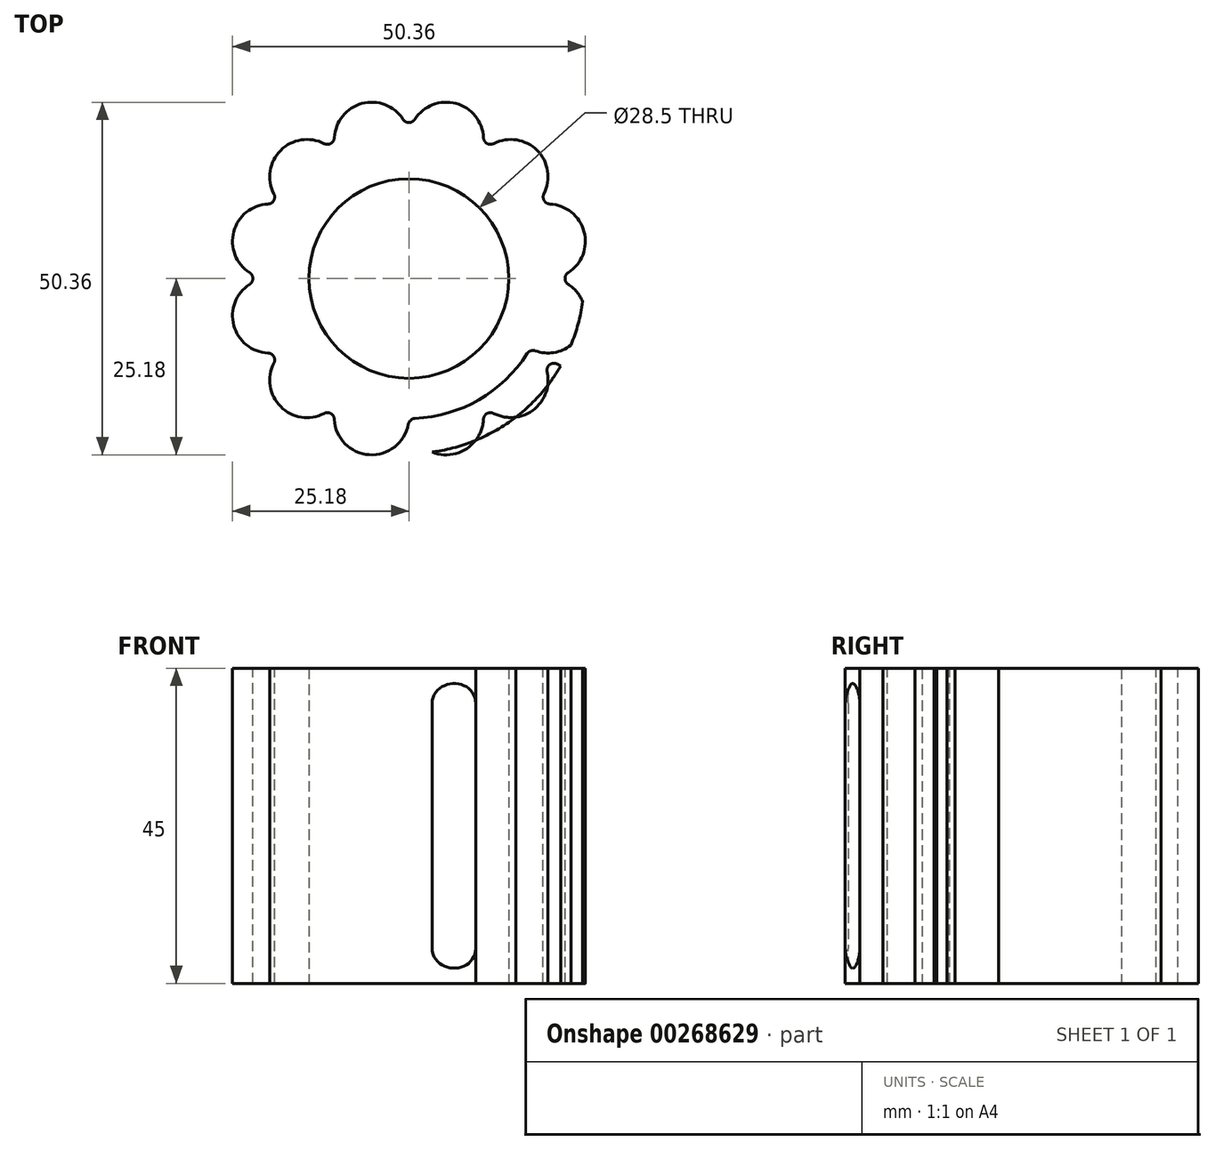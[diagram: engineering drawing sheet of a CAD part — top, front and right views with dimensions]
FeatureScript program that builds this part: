
annotation { "Feature Type Name" : "Feature", "Feature Type Description" : "" }
export const myFeature = defineFeature(function(context is Context, id is Id, definition is map)
    precondition{}
    {
        {
            var Q0;
            Q0=qCreatedBy(makeId("Top.planeOp"),FACE);
            var sketch = newSketch(context, id + "F0", { "sketchPlane" : qUnion([Q0])});
            skCircle(sketch, "E0", {"center": v(0, 0) * mm, "radius": 22.5 * mm});
            skCircle(sketch, "E1", {"center": v(0, 0) * mm, "radius": 14.25 * mm});
            skCircle(sketch, "E2.cCircle", {"center": v(0, 0) * mm, "radius": 22.5 * mm, "construction": true});
            skCircle(sketch, "E3", {"center": v(0, 0) * mm, "radius": 20 * mm});
            skCircle(sketch, "E4.cCircle", {"center": v(0, 0) * mm, "radius": 20 * mm, "construction": true});
            skCircle(sketch, "E5", {"center": v(0, 0) * mm, "radius": 25 * mm});
            skPoint(sketch, "E6.0.midPoint", {"position": v(22.5, 0) * mm});
            skLineSegment(sketch, "E7", {"start": v(-22.5, 12.99) * mm, "end": v(22.5, -12.99) * mm});
            skPoint(sketch, "E8.0.midPoint", {"position": v(11.25, 19.49) * mm});
            skCircle(sketch, "E9.cCircle", {"center": v(0, 0) * mm, "radius": 25 * mm, "construction": true});
            skPoint(sketch, "E9.0.midPoint", {"position": v(0, 25) * mm});
            skArc(sketch, "E10", {"start": v(10, 17.32) * mm, "mid": v(6.7, 25) * mm, "end": v(0, 20) * mm});
            skArc(sketch, "E11", {"start": v(17.32, 10) * mm, "mid": v(18.3, 18.3) * mm, "end": v(10, 17.32) * mm});
            skArc(sketch, "E12", {"start": v(20, 0) * mm, "mid": v(25, 6.7) * mm, "end": v(17.32, 10) * mm});
            skArc(sketch, "E13", {"start": v(17.32, -10) * mm, "mid": v(25, -6.7) * mm, "end": v(20, 0) * mm});
            skArc(sketch, "E14", {"start": v(10, -17.32) * mm, "mid": v(18.3, -18.3) * mm, "end": v(17.32, -10) * mm});
            skArc(sketch, "E15", {"start": v(0, -20) * mm, "mid": v(6.7, -25) * mm, "end": v(10, -17.32) * mm});
            skArc(sketch, "E16", {"start": v(-10, -17.32) * mm, "mid": v(-6.7, -25) * mm, "end": v(0, -20) * mm});
            skArc(sketch, "E17", {"start": v(-17.32, -10) * mm, "mid": v(-18.3, -18.3) * mm, "end": v(-10, -17.32) * mm});
            skArc(sketch, "E18", {"start": v(-20, 0) * mm, "mid": v(-25, -6.7) * mm, "end": v(-17.32, -10) * mm});
            skArc(sketch, "E19", {"start": v(-17.32, 10) * mm, "mid": v(-25, 6.7) * mm, "end": v(-20, 0) * mm});
            skArc(sketch, "E20", {"start": v(-10, 17.32) * mm, "mid": v(-18.3, 18.3) * mm, "end": v(-17.32, 10) * mm});
            skArc(sketch, "E21", {"start": v(0, 20) * mm, "mid": v(-6.7, 25) * mm, "end": v(-10, 17.32) * mm});
            skSolve(sketch);
        }
        {
            var Q0;
            {var subQ0=sQuery(id+"F0.wireOp",EDGE,"E20");var subQ1=sQuery(id+"F0.wireOp",EDGE,"E5");var subQ2=makeQuery(id+"F0.imprint","INTERSECT",VERTEX,{"disambiguationData":[OD(0.0)],"derivedFrom":[subQ1,subQ0]});Q0=makeQuery(id+"F0.imprint","IMPRINT",FACE,{"disambiguationData":[TD([[makeQuery(id+"F0.imprint","IMPRINT",EDGE,{"disambiguationData":[TD([[subQ2,-1.0]])],"derivedFrom":subQ1}),-1.0]])]});}
            var Q1;
            {var subQ0=sQuery(id+"F0.wireOp",EDGE,"E20");var subQ1=sQuery(id+"F0.wireOp",EDGE,"E0");var subQ2=makeQuery(id+"F0.imprint","INTERSECT",VERTEX,{"disambiguationData":[OD(0.0)],"derivedFrom":[subQ1,subQ0]});Q1=makeQuery(id+"F0.imprint","IMPRINT",FACE,{"disambiguationData":[TD([[makeQuery(id+"F0.imprint","IMPRINT",EDGE,{"disambiguationData":[TD([[subQ2,-1.0]])],"derivedFrom":subQ1}),-1.0]])]});}
            var Q2;
            {var subQ0=sQuery(id+"F0.wireOp",EDGE,"E20");var subQ1=sQuery(id+"F0.wireOp",EDGE,"E0");var subQ2=makeQuery(id+"F0.imprint","INTERSECT",VERTEX,{"disambiguationData":[OD(0.0)],"derivedFrom":[subQ1,subQ0]});Q2=makeQuery(id+"F0.imprint","IMPRINT",FACE,{"disambiguationData":[TD([[makeQuery(id+"F0.imprint","IMPRINT",EDGE,{"disambiguationData":[TD([[subQ2,-1.0]])],"derivedFrom":subQ1}),1.0]])]});}
            var Q3;
            {var subQ10=sQuery(id+"F0.wireOp",EDGE,"E7");var subQ12=sQuery(id+"F0.wireOp",EDGE,"E1");var subQ13=makeQuery(id+"F0.imprint","INTERSECT",VERTEX,{"disambiguationData":[OD(0.0)],"derivedFrom":[subQ12,subQ10]});Q3=makeQuery(id+"F0.imprint","IMPRINT",FACE,{"disambiguationData":[TD([[makeQuery(id+"F0.imprint","IMPRINT",EDGE,{"disambiguationData":[TD([[subQ13,1.0]])],"derivedFrom":subQ12}),-1.0]])]});}
            var Q4;
            {var subQ0=sQuery(id+"F0.wireOp",EDGE,"E19");var subQ1=sQuery(id+"F0.wireOp",EDGE,"E5");var subQ2=makeQuery(id+"F0.imprint","INTERSECT",VERTEX,{"disambiguationData":[OD(0.0)],"derivedFrom":[subQ1,subQ0]});Q4=makeQuery(id+"F0.imprint","IMPRINT",FACE,{"disambiguationData":[TD([[makeQuery(id+"F0.imprint","IMPRINT",EDGE,{"disambiguationData":[TD([[subQ2,-1.0]])],"derivedFrom":subQ1}),-1.0]])]});}
            var Q5;
            {var subQ0=sQuery(id+"F0.wireOp",EDGE,"E19");var subQ1=sQuery(id+"F0.wireOp",EDGE,"E0");var subQ2=makeQuery(id+"F0.imprint","INTERSECT",VERTEX,{"disambiguationData":[OD(0.0)],"derivedFrom":[subQ1,subQ0]});Q5=makeQuery(id+"F0.imprint","IMPRINT",FACE,{"disambiguationData":[TD([[makeQuery(id+"F0.imprint","IMPRINT",EDGE,{"disambiguationData":[TD([[subQ2,-1.0]])],"derivedFrom":subQ1}),-1.0]])]});}
            var Q6;
            {var subQ0=sQuery(id+"F0.wireOp",EDGE,"E19");var subQ1=sQuery(id+"F0.wireOp",EDGE,"E0");var subQ2=makeQuery(id+"F0.imprint","INTERSECT",VERTEX,{"disambiguationData":[OD(0.0)],"derivedFrom":[subQ1,subQ0]});Q6=makeQuery(id+"F0.imprint","IMPRINT",FACE,{"disambiguationData":[TD([[makeQuery(id+"F0.imprint","IMPRINT",EDGE,{"disambiguationData":[TD([[subQ2,-1.0]])],"derivedFrom":subQ1}),1.0]])]});}
            var Q7;
            {var subQ0=sQuery(id+"F0.wireOp",EDGE,"E18");var subQ1=sQuery(id+"F0.wireOp",EDGE,"E5");var subQ2=makeQuery(id+"F0.imprint","INTERSECT",VERTEX,{"disambiguationData":[OD(0.0)],"derivedFrom":[subQ1,subQ0]});Q7=makeQuery(id+"F0.imprint","IMPRINT",FACE,{"disambiguationData":[TD([[makeQuery(id+"F0.imprint","IMPRINT",EDGE,{"disambiguationData":[TD([[subQ2,-1.0]])],"derivedFrom":subQ1}),-1.0]])]});}
            var Q8;
            {var subQ0=sQuery(id+"F0.wireOp",EDGE,"E18");var subQ1=sQuery(id+"F0.wireOp",EDGE,"E0");var subQ2=makeQuery(id+"F0.imprint","INTERSECT",VERTEX,{"disambiguationData":[OD(0.0)],"derivedFrom":[subQ1,subQ0]});Q8=makeQuery(id+"F0.imprint","IMPRINT",FACE,{"disambiguationData":[TD([[makeQuery(id+"F0.imprint","IMPRINT",EDGE,{"disambiguationData":[TD([[subQ2,-1.0]])],"derivedFrom":subQ1}),-1.0]])]});}
            var Q9;
            {var subQ0=sQuery(id+"F0.wireOp",EDGE,"E18");var subQ1=sQuery(id+"F0.wireOp",EDGE,"E0");var subQ2=makeQuery(id+"F0.imprint","INTERSECT",VERTEX,{"disambiguationData":[OD(0.0)],"derivedFrom":[subQ1,subQ0]});Q9=makeQuery(id+"F0.imprint","IMPRINT",FACE,{"disambiguationData":[TD([[makeQuery(id+"F0.imprint","IMPRINT",EDGE,{"disambiguationData":[TD([[subQ2,-1.0]])],"derivedFrom":subQ1}),1.0]])]});}
            var Q10;
            {var subQ0=sQuery(id+"F0.wireOp",EDGE,"E17");var subQ1=sQuery(id+"F0.wireOp",EDGE,"E5");var subQ2=makeQuery(id+"F0.imprint","INTERSECT",VERTEX,{"disambiguationData":[OD(0.0)],"derivedFrom":[subQ1,subQ0]});Q10=makeQuery(id+"F0.imprint","IMPRINT",FACE,{"disambiguationData":[TD([[makeQuery(id+"F0.imprint","IMPRINT",EDGE,{"disambiguationData":[TD([[subQ2,-1.0]])],"derivedFrom":subQ1}),-1.0]])]});}
            var Q11;
            {var subQ0=sQuery(id+"F0.wireOp",EDGE,"E17");var subQ1=sQuery(id+"F0.wireOp",EDGE,"E0");var subQ2=makeQuery(id+"F0.imprint","INTERSECT",VERTEX,{"disambiguationData":[OD(0.0)],"derivedFrom":[subQ1,subQ0]});Q11=makeQuery(id+"F0.imprint","IMPRINT",FACE,{"disambiguationData":[TD([[makeQuery(id+"F0.imprint","IMPRINT",EDGE,{"disambiguationData":[TD([[subQ2,-1.0]])],"derivedFrom":subQ1}),-1.0]])]});}
            var Q12;
            {var subQ0=sQuery(id+"F0.wireOp",EDGE,"E17");var subQ1=sQuery(id+"F0.wireOp",EDGE,"E0");var subQ2=makeQuery(id+"F0.imprint","INTERSECT",VERTEX,{"disambiguationData":[OD(0.0)],"derivedFrom":[subQ1,subQ0]});Q12=makeQuery(id+"F0.imprint","IMPRINT",FACE,{"disambiguationData":[TD([[makeQuery(id+"F0.imprint","IMPRINT",EDGE,{"disambiguationData":[TD([[subQ2,-1.0]])],"derivedFrom":subQ1}),1.0]])]});}
            var Q13;
            {var subQ0=sQuery(id+"F0.wireOp",EDGE,"E21");var subQ1=sQuery(id+"F0.wireOp",EDGE,"E5");var subQ2=makeQuery(id+"F0.imprint","INTERSECT",VERTEX,{"disambiguationData":[OD(0.0)],"derivedFrom":[subQ1,subQ0]});Q13=makeQuery(id+"F0.imprint","IMPRINT",FACE,{"disambiguationData":[TD([[makeQuery(id+"F0.imprint","IMPRINT",EDGE,{"disambiguationData":[TD([[subQ2,-1.0]])],"derivedFrom":subQ1}),-1.0]])]});}
            var Q14;
            {var subQ0=sQuery(id+"F0.wireOp",EDGE,"E21");var subQ1=sQuery(id+"F0.wireOp",EDGE,"E0");var subQ2=makeQuery(id+"F0.imprint","INTERSECT",VERTEX,{"disambiguationData":[OD(0.0)],"derivedFrom":[subQ1,subQ0]});Q14=makeQuery(id+"F0.imprint","IMPRINT",FACE,{"disambiguationData":[TD([[makeQuery(id+"F0.imprint","IMPRINT",EDGE,{"disambiguationData":[TD([[subQ2,-1.0]])],"derivedFrom":subQ1}),-1.0]])]});}
            var Q15;
            {var subQ0=sQuery(id+"F0.wireOp",EDGE,"E21");var subQ1=sQuery(id+"F0.wireOp",EDGE,"E0");var subQ2=makeQuery(id+"F0.imprint","INTERSECT",VERTEX,{"disambiguationData":[OD(0.0)],"derivedFrom":[subQ1,subQ0]});Q15=makeQuery(id+"F0.imprint","IMPRINT",FACE,{"disambiguationData":[TD([[makeQuery(id+"F0.imprint","IMPRINT",EDGE,{"disambiguationData":[TD([[subQ2,-1.0]])],"derivedFrom":subQ1}),1.0]])]});}
            var Q16;
            {var subQ0=sQuery(id+"F0.wireOp",EDGE,"E10");var subQ1=sQuery(id+"F0.wireOp",EDGE,"E0");var subQ2=makeQuery(id+"F0.imprint","INTERSECT",VERTEX,{"disambiguationData":[OD(0.0)],"derivedFrom":[subQ1,subQ0]});Q16=makeQuery(id+"F0.imprint","IMPRINT",FACE,{"disambiguationData":[TD([[makeQuery(id+"F0.imprint","IMPRINT",EDGE,{"disambiguationData":[TD([[subQ2,-1.0]])],"derivedFrom":subQ1}),1.0]])]});}
            var Q17;
            {var subQ0=sQuery(id+"F0.wireOp",EDGE,"E10");var subQ1=sQuery(id+"F0.wireOp",EDGE,"E0");var subQ2=makeQuery(id+"F0.imprint","INTERSECT",VERTEX,{"disambiguationData":[OD(0.0)],"derivedFrom":[subQ1,subQ0]});Q17=makeQuery(id+"F0.imprint","IMPRINT",FACE,{"disambiguationData":[TD([[makeQuery(id+"F0.imprint","IMPRINT",EDGE,{"disambiguationData":[TD([[subQ2,-1.0]])],"derivedFrom":subQ1}),-1.0]])]});}
            var Q18;
            {var subQ0=sQuery(id+"F0.wireOp",EDGE,"E10");var subQ1=sQuery(id+"F0.wireOp",EDGE,"E5");var subQ2=makeQuery(id+"F0.imprint","INTERSECT",VERTEX,{"disambiguationData":[OD(0.0)],"derivedFrom":[subQ1,subQ0]});Q18=makeQuery(id+"F0.imprint","IMPRINT",FACE,{"disambiguationData":[TD([[makeQuery(id+"F0.imprint","IMPRINT",EDGE,{"disambiguationData":[TD([[subQ2,-1.0]])],"derivedFrom":subQ1}),-1.0]])]});}
            var Q19;
            {var subQ0=sQuery(id+"F0.wireOp",EDGE,"E11");var subQ1=sQuery(id+"F0.wireOp",EDGE,"E0");var subQ2=makeQuery(id+"F0.imprint","INTERSECT",VERTEX,{"disambiguationData":[OD(0.0)],"derivedFrom":[subQ1,subQ0]});Q19=makeQuery(id+"F0.imprint","IMPRINT",FACE,{"disambiguationData":[TD([[makeQuery(id+"F0.imprint","IMPRINT",EDGE,{"disambiguationData":[TD([[subQ2,-1.0]])],"derivedFrom":subQ1}),1.0]])]});}
            var Q20;
            {var subQ0=sQuery(id+"F0.wireOp",EDGE,"E11");var subQ1=sQuery(id+"F0.wireOp",EDGE,"E0");var subQ2=makeQuery(id+"F0.imprint","INTERSECT",VERTEX,{"disambiguationData":[OD(0.0)],"derivedFrom":[subQ1,subQ0]});Q20=makeQuery(id+"F0.imprint","IMPRINT",FACE,{"disambiguationData":[TD([[makeQuery(id+"F0.imprint","IMPRINT",EDGE,{"disambiguationData":[TD([[subQ2,-1.0]])],"derivedFrom":subQ1}),-1.0]])]});}
            var Q21;
            {var subQ0=sQuery(id+"F0.wireOp",EDGE,"E11");var subQ1=sQuery(id+"F0.wireOp",EDGE,"E5");var subQ2=makeQuery(id+"F0.imprint","INTERSECT",VERTEX,{"disambiguationData":[OD(0.0)],"derivedFrom":[subQ1,subQ0]});Q21=makeQuery(id+"F0.imprint","IMPRINT",FACE,{"disambiguationData":[TD([[makeQuery(id+"F0.imprint","IMPRINT",EDGE,{"disambiguationData":[TD([[subQ2,-1.0]])],"derivedFrom":subQ1}),-1.0]])]});}
            var Q22;
            {var subQ0=sQuery(id+"F0.wireOp",EDGE,"E12");var subQ1=sQuery(id+"F0.wireOp",EDGE,"E0");var subQ2=makeQuery(id+"F0.imprint","INTERSECT",VERTEX,{"disambiguationData":[OD(0.0)],"derivedFrom":[subQ1,subQ0]});Q22=makeQuery(id+"F0.imprint","IMPRINT",FACE,{"disambiguationData":[TD([[makeQuery(id+"F0.imprint","IMPRINT",EDGE,{"disambiguationData":[TD([[subQ2,1.0]])],"derivedFrom":subQ1}),1.0]])]});}
            var Q23;
            {var subQ0=sQuery(id+"F0.wireOp",EDGE,"E12");var subQ1=sQuery(id+"F0.wireOp",EDGE,"E0");var subQ2=makeQuery(id+"F0.imprint","INTERSECT",VERTEX,{"disambiguationData":[OD(0.0)],"derivedFrom":[subQ1,subQ0]});Q23=makeQuery(id+"F0.imprint","IMPRINT",FACE,{"disambiguationData":[TD([[makeQuery(id+"F0.imprint","IMPRINT",EDGE,{"disambiguationData":[TD([[subQ2,1.0]])],"derivedFrom":subQ1}),-1.0]])]});}
            var Q24;
            {var subQ0=sQuery(id+"F0.wireOp",EDGE,"E12");var subQ1=sQuery(id+"F0.wireOp",EDGE,"E5");var subQ2=makeQuery(id+"F0.imprint","INTERSECT",VERTEX,{"disambiguationData":[OD(0.0)],"derivedFrom":[subQ1,subQ0]});Q24=makeQuery(id+"F0.imprint","IMPRINT",FACE,{"disambiguationData":[TD([[makeQuery(id+"F0.imprint","IMPRINT",EDGE,{"disambiguationData":[TD([[subQ2,1.0]])],"derivedFrom":subQ1}),-1.0]])]});}
            var Q25;
            {var subQ0=sQuery(id+"F0.wireOp",EDGE,"E13");var subQ1=sQuery(id+"F0.wireOp",EDGE,"E0");var subQ2=makeQuery(id+"F0.imprint","INTERSECT",VERTEX,{"disambiguationData":[OD(0.0)],"derivedFrom":[subQ1,subQ0]});Q25=makeQuery(id+"F0.imprint","IMPRINT",FACE,{"disambiguationData":[TD([[makeQuery(id+"F0.imprint","IMPRINT",EDGE,{"disambiguationData":[TD([[subQ2,-1.0]])],"derivedFrom":subQ1}),-1.0]])]});}
            var Q26;
            {var subQ0=sQuery(id+"F0.wireOp",EDGE,"E13");var subQ1=sQuery(id+"F0.wireOp",EDGE,"E5");var subQ2=makeQuery(id+"F0.imprint","INTERSECT",VERTEX,{"disambiguationData":[OD(0.0)],"derivedFrom":[subQ1,subQ0]});Q26=makeQuery(id+"F0.imprint","IMPRINT",FACE,{"disambiguationData":[TD([[makeQuery(id+"F0.imprint","IMPRINT",EDGE,{"disambiguationData":[TD([[subQ2,-1.0]])],"derivedFrom":subQ1}),-1.0]])]});}
            var Q27;
            {var subQ0=sQuery(id+"F0.wireOp",EDGE,"E14");var subQ1=sQuery(id+"F0.wireOp",EDGE,"E0");var subQ2=makeQuery(id+"F0.imprint","INTERSECT",VERTEX,{"disambiguationData":[OD(0.0)],"derivedFrom":[subQ1,subQ0]});Q27=makeQuery(id+"F0.imprint","IMPRINT",FACE,{"disambiguationData":[TD([[makeQuery(id+"F0.imprint","IMPRINT",EDGE,{"disambiguationData":[TD([[subQ2,-1.0]])],"derivedFrom":subQ1}),1.0]])]});}
            var Q28;
            {var subQ0=sQuery(id+"F0.wireOp",EDGE,"E14");var subQ1=sQuery(id+"F0.wireOp",EDGE,"E0");var subQ2=makeQuery(id+"F0.imprint","INTERSECT",VERTEX,{"disambiguationData":[OD(0.0)],"derivedFrom":[subQ1,subQ0]});Q28=makeQuery(id+"F0.imprint","IMPRINT",FACE,{"disambiguationData":[TD([[makeQuery(id+"F0.imprint","IMPRINT",EDGE,{"disambiguationData":[TD([[subQ2,-1.0]])],"derivedFrom":subQ1}),-1.0]])]});}
            var Q29;
            {var subQ0=sQuery(id+"F0.wireOp",EDGE,"E14");var subQ1=sQuery(id+"F0.wireOp",EDGE,"E5");var subQ2=makeQuery(id+"F0.imprint","INTERSECT",VERTEX,{"disambiguationData":[OD(0.0)],"derivedFrom":[subQ1,subQ0]});Q29=makeQuery(id+"F0.imprint","IMPRINT",FACE,{"disambiguationData":[TD([[makeQuery(id+"F0.imprint","IMPRINT",EDGE,{"disambiguationData":[TD([[subQ2,-1.0]])],"derivedFrom":subQ1}),-1.0]])]});}
            var Q30;
            {var subQ0=sQuery(id+"F0.wireOp",EDGE,"E15");var subQ1=sQuery(id+"F0.wireOp",EDGE,"E0");var subQ2=makeQuery(id+"F0.imprint","INTERSECT",VERTEX,{"disambiguationData":[OD(0.0)],"derivedFrom":[subQ1,subQ0]});Q30=makeQuery(id+"F0.imprint","IMPRINT",FACE,{"disambiguationData":[TD([[makeQuery(id+"F0.imprint","IMPRINT",EDGE,{"disambiguationData":[TD([[subQ2,-1.0]])],"derivedFrom":subQ1}),1.0]])]});}
            var Q31;
            {var subQ0=sQuery(id+"F0.wireOp",EDGE,"E16");var subQ1=sQuery(id+"F0.wireOp",EDGE,"E0");var subQ2=makeQuery(id+"F0.imprint","INTERSECT",VERTEX,{"disambiguationData":[OD(0.0)],"derivedFrom":[subQ1,subQ0]});Q31=makeQuery(id+"F0.imprint","IMPRINT",FACE,{"disambiguationData":[TD([[makeQuery(id+"F0.imprint","IMPRINT",EDGE,{"disambiguationData":[TD([[subQ2,-1.0]])],"derivedFrom":subQ1}),-1.0]])]});}
            var Q32;
            {var subQ7=sQuery(id+"F0.wireOp",EDGE,"E7");var subQ9=sQuery(id+"F0.wireOp",EDGE,"E1");var subQ10=makeQuery(id+"F0.imprint","INTERSECT",VERTEX,{"disambiguationData":[OD(0.0)],"derivedFrom":[subQ9,subQ7]});Q32=makeQuery(id+"F0.imprint","IMPRINT",FACE,{"disambiguationData":[TD([[makeQuery(id+"F0.imprint","IMPRINT",EDGE,{"disambiguationData":[TD([[subQ10,-1.0]])],"derivedFrom":subQ9}),-1.0]])]});}
            var Q33;
            {var subQ0=sQuery(id+"F0.wireOp",EDGE,"E16");var subQ1=sQuery(id+"F0.wireOp",EDGE,"E0");var subQ2=makeQuery(id+"F0.imprint","INTERSECT",VERTEX,{"disambiguationData":[OD(0.0)],"derivedFrom":[subQ1,subQ0]});Q33=makeQuery(id+"F0.imprint","IMPRINT",FACE,{"disambiguationData":[TD([[makeQuery(id+"F0.imprint","IMPRINT",EDGE,{"disambiguationData":[TD([[subQ2,-1.0]])],"derivedFrom":subQ1}),1.0]])]});}
            var Q34;
            {var subQ0=sQuery(id+"F0.wireOp",EDGE,"E15");var subQ1=sQuery(id+"F0.wireOp",EDGE,"E0");var subQ2=makeQuery(id+"F0.imprint","INTERSECT",VERTEX,{"disambiguationData":[OD(0.0)],"derivedFrom":[subQ1,subQ0]});Q34=makeQuery(id+"F0.imprint","IMPRINT",FACE,{"disambiguationData":[TD([[makeQuery(id+"F0.imprint","IMPRINT",EDGE,{"disambiguationData":[TD([[subQ2,-1.0]])],"derivedFrom":subQ1}),-1.0]])]});}
            var Q35;
            {var subQ0=sQuery(id+"F0.wireOp",EDGE,"E15");var subQ1=sQuery(id+"F0.wireOp",EDGE,"E5");var subQ2=makeQuery(id+"F0.imprint","INTERSECT",VERTEX,{"disambiguationData":[OD(0.0)],"derivedFrom":[subQ1,subQ0]});Q35=makeQuery(id+"F0.imprint","IMPRINT",FACE,{"disambiguationData":[TD([[makeQuery(id+"F0.imprint","IMPRINT",EDGE,{"disambiguationData":[TD([[subQ2,-1.0]])],"derivedFrom":subQ1}),-1.0]])]});}
            var Q36;
            {var subQ0=sQuery(id+"F0.wireOp",EDGE,"E16");var subQ1=sQuery(id+"F0.wireOp",EDGE,"E5");var subQ2=makeQuery(id+"F0.imprint","INTERSECT",VERTEX,{"disambiguationData":[OD(0.0)],"derivedFrom":[subQ1,subQ0]});Q36=makeQuery(id+"F0.imprint","IMPRINT",FACE,{"disambiguationData":[TD([[makeQuery(id+"F0.imprint","IMPRINT",EDGE,{"disambiguationData":[TD([[subQ2,-1.0]])],"derivedFrom":subQ1}),-1.0]])]});}
            var Q37;
            {var subQ0=sQuery(id+"F0.wireOp",EDGE,"E13");var subQ1=sQuery(id+"F0.wireOp",EDGE,"E0");var subQ2=makeQuery(id+"F0.imprint","INTERSECT",VERTEX,{"disambiguationData":[OD(0.0)],"derivedFrom":[subQ1,subQ0]});Q37=makeQuery(id+"F0.imprint","IMPRINT",FACE,{"disambiguationData":[TD([[makeQuery(id+"F0.imprint","IMPRINT",EDGE,{"disambiguationData":[TD([[subQ2,-1.0]])],"derivedFrom":subQ1}),1.0]])]});}
            extrude(context, id + "F1", {"entities" : qUnion([Q0, Q1, Q2, Q3, Q4, Q5, Q6, Q7, Q8, Q9, Q10, Q11, Q12, Q13, Q14, Q15, Q16, Q17, Q18, Q19, Q20, Q21, Q22, Q23, Q24, Q25, Q26, Q27, Q28, Q29, Q30, Q31, Q32, Q33, Q34, Q35, Q36, Q37]), "depth" : 45 * mm, "offsetDistance" : 25 * mm});
        }
        {
            var Q0;
            Q0=makeQuery(id+"F1.opExtrude","SWEPT_EDGE",EDGE,{"disambiguationData":[OSD([sQuery(id+"F0.wireOp",EDGE,"E3"),sQuery(id+"F0.wireOp",EDGE,"E14"),sQuery(id+"F0.wireOp",EDGE,"E15")])]});
            var Q1;
            Q1=makeQuery(id+"F1.opExtrude","SWEPT_EDGE",EDGE,{"disambiguationData":[OSD([sQuery(id+"F0.wireOp",EDGE,"E3"),sQuery(id+"F0.wireOp",EDGE,"E7"),sQuery(id+"F0.wireOp",EDGE,"E13"),sQuery(id+"F0.wireOp",EDGE,"E14")])]});
            var Q2;
            Q2=makeQuery(id+"F1.opExtrude","SWEPT_EDGE",EDGE,{"disambiguationData":[OSD([sQuery(id+"F0.wireOp",EDGE,"E3"),sQuery(id+"F0.wireOp",EDGE,"E12"),sQuery(id+"F0.wireOp",EDGE,"E13")])]});
            var Q3;
            Q3=makeQuery(id+"F1.opExtrude","SWEPT_EDGE",EDGE,{"disambiguationData":[OSD([sQuery(id+"F0.wireOp",EDGE,"E3"),sQuery(id+"F0.wireOp",EDGE,"E11"),sQuery(id+"F0.wireOp",EDGE,"E12")])]});
            var Q4;
            Q4=makeQuery(id+"F1.opExtrude","SWEPT_EDGE",EDGE,{"disambiguationData":[OSD([sQuery(id+"F0.wireOp",EDGE,"E3"),sQuery(id+"F0.wireOp",EDGE,"E7"),sQuery(id+"F0.wireOp",EDGE,"E19"),sQuery(id+"F0.wireOp",EDGE,"E20")])]});
            var Q5;
            Q5=makeQuery(id+"F1.opExtrude","SWEPT_EDGE",EDGE,{"disambiguationData":[OSD([sQuery(id+"F0.wireOp",EDGE,"E3"),sQuery(id+"F0.wireOp",EDGE,"E10"),sQuery(id+"F0.wireOp",EDGE,"E21")])]});
            var Q6;
            Q6=makeQuery(id+"F1.opExtrude","SWEPT_EDGE",EDGE,{"disambiguationData":[OSD([sQuery(id+"F0.wireOp",EDGE,"E3"),sQuery(id+"F0.wireOp",EDGE,"E10"),sQuery(id+"F0.wireOp",EDGE,"E11")])]});
            var Q7;
            Q7=makeQuery(id+"F1.opExtrude","SWEPT_EDGE",EDGE,{"disambiguationData":[OSD([sQuery(id+"F0.wireOp",EDGE,"E3"),sQuery(id+"F0.wireOp",EDGE,"E20"),sQuery(id+"F0.wireOp",EDGE,"E21")])]});
            var Q8;
            Q8=makeQuery(id+"F1.opExtrude","SWEPT_EDGE",EDGE,{"disambiguationData":[OSD([sQuery(id+"F0.wireOp",EDGE,"E3"),sQuery(id+"F0.wireOp",EDGE,"E18"),sQuery(id+"F0.wireOp",EDGE,"E19")])]});
            var Q9;
            Q9=makeQuery(id+"F1.opExtrude","SWEPT_EDGE",EDGE,{"disambiguationData":[OSD([sQuery(id+"F0.wireOp",EDGE,"E3"),sQuery(id+"F0.wireOp",EDGE,"E17"),sQuery(id+"F0.wireOp",EDGE,"E18")])]});
            var Q10;
            Q10=makeQuery(id+"F1.opExtrude","SWEPT_EDGE",EDGE,{"disambiguationData":[OSD([sQuery(id+"F0.wireOp",EDGE,"E3"),sQuery(id+"F0.wireOp",EDGE,"E16"),sQuery(id+"F0.wireOp",EDGE,"E17")])]});
            var Q11;
            Q11=makeQuery(id+"F1.opExtrude","SWEPT_EDGE",EDGE,{"disambiguationData":[OSD([sQuery(id+"F0.wireOp",EDGE,"E3"),sQuery(id+"F0.wireOp",EDGE,"E15"),sQuery(id+"F0.wireOp",EDGE,"E16")])]});
            fillet(context, id + "F2", {"entities" : qUnion([Q0, Q1, Q2, Q3, Q4, Q5, Q6, Q7, Q8, Q9, Q10, Q11]), "radius" : 1 * mm, "allowEdgeOverflow" : false});
        }
        {
            var Q0;
            Q0=makeQuery(id+"F1.opExtrude","CAP_EDGE",EDGE,{"disambiguationData":[OSD([sQuery(id+"F0.wireOp",EDGE,"E15")])],"isStart":true});
            var Q1;
            Q1=makeQuery(id+"F1.opExtrude","CAP_EDGE",EDGE,{"disambiguationData":[OSD([sQuery(id+"F0.wireOp",EDGE,"E15")])],"isStart":false});
            fillet(context, id + "F3", {"entities" : qUnion([Q0, Q1]), "radius" : 5 * mm, "tangentPropagation" : true, "allowEdgeOverflow" : false});
        }
    });
